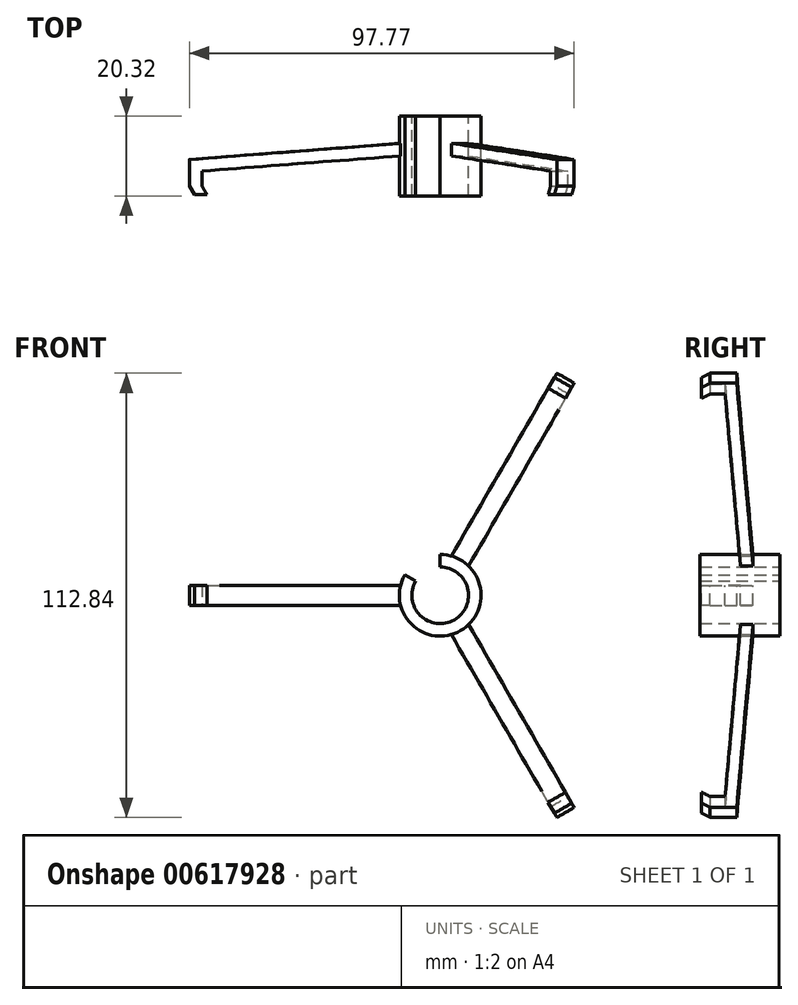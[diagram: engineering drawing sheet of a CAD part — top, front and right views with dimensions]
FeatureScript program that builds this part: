
annotation { "Feature Type Name" : "Feature", "Feature Type Description" : "" }
export const myFeature = defineFeature(function(context is Context, id is Id, definition is map)
    precondition{}
    {
        {
            var Q0;
            Q0=qCreatedBy(makeId("Top.planeOp"),FACE);
            var sketch = newSketch(context, id + "F0", { "sketchPlane" : qUnion([Q0])});
            skLineSegment(sketch, "E0", {"start": v(63.73, 2.94) * mm, "end": v(63.73, -3.81) * mm});
            skLineSegment(sketch, "E1", {"start": v(60.55, -3.81) * mm, "end": v(60.55, 0) * mm});
            skLineSegment(sketch, "E2", {"start": v(60.55, 0) * mm, "end": v(10.38, 3.86) * mm});
            skLineSegment(sketch, "E3", {"start": v(10.38, 3.86) * mm, "end": v(10.38, -6.35) * mm});
            skLineSegment(sketch, "E4", {"start": v(10.38, -6.35) * mm, "end": v(7.2, -6.35) * mm});
            skLineSegment(sketch, "E5", {"start": v(7.2, -6.35) * mm, "end": v(7.2, 13.97) * mm});
            skLineSegment(sketch, "E6", {"start": v(7.2, 13.97) * mm, "end": v(10.38, 13.97) * mm});
            skLineSegment(sketch, "E7", {"start": v(10.38, 13.97) * mm, "end": v(10.38, 7.05) * mm});
            skLineSegment(sketch, "E8", {"start": v(10.38, 7.05) * mm, "end": v(63.73, 2.94) * mm});
            skLineSegment(sketch, "E9", {"start": v(0, 0) * mm, "end": v(60.55, 0) * mm, "construction": true});
            skLineSegment(sketch, "E10", {"start": v(60.55, -3.8) * mm, "end": v(59.28, -6) * mm});
            skLineSegment(sketch, "E11", {"start": v(59.28, -6) * mm, "end": v(62.46, -6) * mm});
            skLineSegment(sketch, "E12", {"start": v(62.46, -6) * mm, "end": v(63.73, -3.81) * mm});
            skLineSegment(sketch, "E13", {"start": v(0, 7.57) * mm, "end": v(7.2, 7.57) * mm, "construction": true});
            skLineSegment(sketch, "E14", {"start": v(0, 7.57) * mm, "end": v(0, -33.98) * mm, "construction": true});
            skSolve(sketch);
        }
        {
            var Q0;
            Q0 = qSketchRegion(id + "F0", true);
            var Q1;
            Q1=sQuery(id+"F0.wireOp",EDGE,"E14");
            revolve(context, id + "F1", {"entities" : qUnion([Q0]), "axis" : qUnion([Q1]), "revolveType" : RevolveType.FULL});
        }
        {
            var Q0;
            Q0=makeQuery(id+"F1.opRevolve","SWEPT_FACE",FACE,{"disambiguationData":[OSD([sQuery(id+"F0.wireOp",EDGE,"E6")])]});
            var sketch = newSketch(context, id + "F2", { "sketchPlane" : qUnion([Q0])});
            skLineSegment(sketch, "E15", {"start": v(10.06, -2.54) * mm, "end": v(111.03, -2.54) * mm});
            skLineSegment(sketch, "E16", {"start": v(111.03, -2.54) * mm, "end": v(111.03, 2.54) * mm, "construction": true});
            skLineSegment(sketch, "E17", {"start": v(111.03, 2.54) * mm, "end": v(10.06, 2.54) * mm});
            skPoint(sketch, "E18", {"position": v(111.03, 0) * mm});
            skArc(sketch, "E19", {"start": v(10.06, 2.54) * mm, "mid": v(9.61, 3.9) * mm, "end": v(8.99, 5.19) * mm});
            skLineSegment(sketch, "E20.1.0", {"start": v(-2.83, 9.98) * mm, "end": v(-53.31, 97.42) * mm});
            skLineSegment(sketch, "E20.1.1", {"start": v(-57.71, 94.88) * mm, "end": v(-7.23, 7.44) * mm});
            skLineSegment(sketch, "E20.2.0", {"start": v(-7.23, -7.44) * mm, "end": v(-57.71, -94.88) * mm});
            skLineSegment(sketch, "E20.2.1", {"start": v(-53.31, -97.42) * mm, "end": v(-2.83, -9.98) * mm});
            skArc(sketch, "E21.trimOffspring", {"start": v(-7.23, 7.44) * mm, "mid": v(-10.38, 0) * mm, "end": v(-7.23, -7.44) * mm});
            skArc(sketch, "E22.trimOffspring", {"start": v(-2.83, -9.98) * mm, "mid": v(5.19, -8.99) * mm, "end": v(10.06, -2.54) * mm});
            skArc(sketch, "E23", {"start": v(111.03, 2.54) * mm, "mid": v(40.76, 70.6) * mm, "end": v(-53.31, 97.42) * mm});
            skArc(sketch, "E24.1.0", {"start": v(-57.71, 94.88) * mm, "mid": v(-81.52, 0) * mm, "end": v(-57.71, -94.88) * mm});
            skArc(sketch, "E24.2.0", {"start": v(-53.31, -97.42) * mm, "mid": v(40.76, -70.6) * mm, "end": v(111.03, -2.54) * mm});
            skLineSegment(sketch, "E25", {"start": v(0, 0) * mm, "end": v(0, 10.38) * mm});
            skLineSegment(sketch, "E26", {"start": v(0, 0) * mm, "end": v(8.99, 5.19) * mm});
            skArc(sketch, "E27.trimOffspring", {"start": v(0, 10.38) * mm, "mid": v(-1.43, 10.28) * mm, "end": v(-2.83, 9.98) * mm});
            skSolve(sketch);
        }
        {
            var Q0;
            Q0 = qSketchRegion(id + "F2", true);
            extrude(context, id + "F3", {"entities" : qUnion([Q0]), "operationType" : NewBodyOperationType.REMOVE, "oppositeDirection" : true, "depth" : 25.4 * mm, "offsetDistance" : 25.4 * mm});
        }
    });
